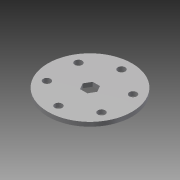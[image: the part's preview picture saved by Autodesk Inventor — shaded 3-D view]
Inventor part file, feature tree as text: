
AUTODESK INVENTOR PART (.ipt)
format: ipt  version: 2013 (Build 170138000, 138)  size: 95,744 bytes
history: native  units: in
note: dims shown in document units (in); Inventor stores cm internally (conversion verified against a paired STEP export)
features: extrude x1, sketch x1
ambient origin geometry x8: Origin, YZ Plane, XZ Plane, XY Plane, X Axis, Y Axis, Z Axis, Center Point
feature tree (2):
  extrude  "Extrusion3"  Depth=0.22in
  sketch  "Sketch1"  dims[d0=0.375in d5=0.22in d7=2.3622in d9=360.0deg d22=0.375in d23=0.125in d24=0.0in d25=0.9375in]
